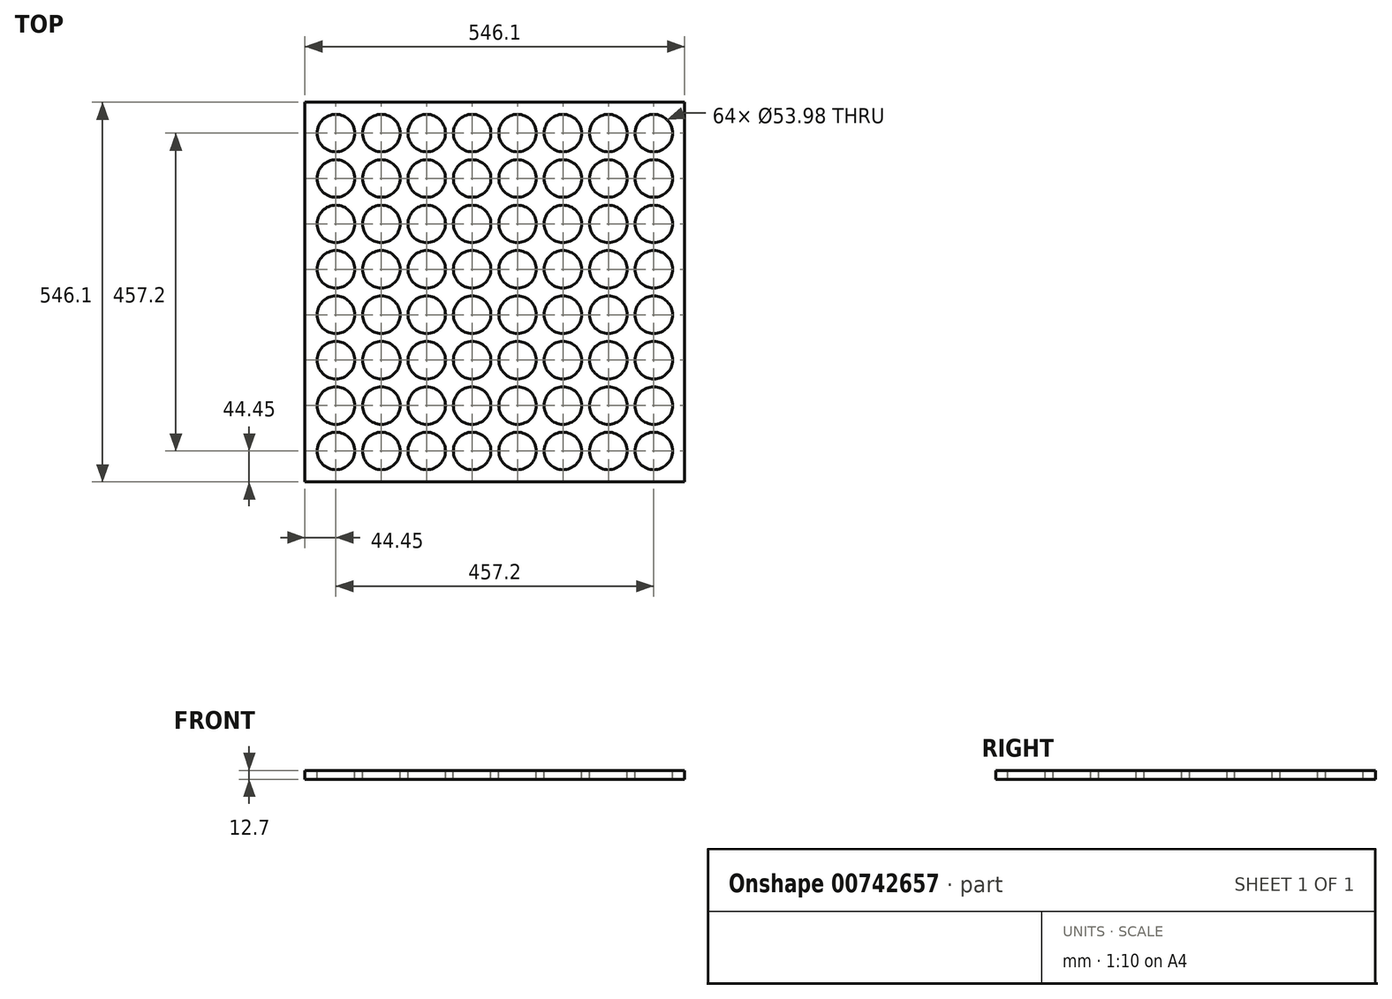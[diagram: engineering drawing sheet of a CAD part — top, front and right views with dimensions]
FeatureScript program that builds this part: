
annotation { "Feature Type Name" : "Feature", "Feature Type Description" : "" }
export const myFeature = defineFeature(function(context is Context, id is Id, definition is map)
    precondition{}
    {
        {
            var Q0;
            Q0=qCreatedBy(makeId("Top.planeOp"),FACE);
            var sketch = newSketch(context, id + "F0", { "sketchPlane" : qUnion([Q0])});
            skLineSegment(sketch, "E0.bottom", {"start": v(-273.05, 273.05) * mm, "end": v(273.05, 273.05) * mm});
            skLineSegment(sketch, "E0.top", {"start": v(-273.05, -273.05) * mm, "end": v(273.05, -273.05) * mm});
            skLineSegment(sketch, "E0.left", {"start": v(-273.05, 273.05) * mm, "end": v(-273.05, -273.05) * mm});
            skLineSegment(sketch, "E0.right", {"start": v(273.05, 273.05) * mm, "end": v(273.05, -273.05) * mm});
            skPoint(sketch, "E0.middle", {"position": v(0, 0) * mm});
            skSolve(sketch);
        }
        {
            var Q0;
            Q0=makeQuery(id+"F0.imprint","IMPRINT",FACE,{"disambiguationData":[TD([[makeQuery(id+"F0.imprint","IMPRINT",EDGE,{"derivedFrom":sQuery(id+"F0.wireOp",EDGE,"E0.bottom")}),-1.0]])]});
            extrude(context, id + "F1", {"entities" : qUnion([Q0]), "depth" : 12.7 * mm, "offsetDistance" : 25.4 * mm});
        }
        {
            var Q0;
            Q0=makeQuery(id+"F1.opExtrude","CAP_FACE",FACE,{"disambiguationData":[OSD([sQuery(id+"F0.wireOp",EDGE,"E0.bottom"),sQuery(id+"F0.wireOp",EDGE,"E0.top"),sQuery(id+"F0.wireOp",EDGE,"E0.left"),sQuery(id+"F0.wireOp",EDGE,"E0.right")])],"isStart":false});
            var sketch = newSketch(context, id + "F2", { "sketchPlane" : qUnion([Q0])});
            skCircle(sketch, "E1", {"center": v(-228.6, 228.6) * mm, "radius": 26.99 * mm});
            skCircle(sketch, "E2.0.1.0", {"center": v(-228.6, 163.29) * mm, "radius": 26.99 * mm});
            skCircle(sketch, "E2.0.2.0", {"center": v(-228.6, 97.97) * mm, "radius": 26.99 * mm});
            skCircle(sketch, "E2.0.3.0", {"center": v(-228.6, 32.66) * mm, "radius": 26.99 * mm});
            skCircle(sketch, "E2.0.4.0", {"center": v(-228.6, -32.66) * mm, "radius": 26.99 * mm});
            skCircle(sketch, "E2.0.5.0", {"center": v(-228.6, -97.97) * mm, "radius": 26.99 * mm});
            skCircle(sketch, "E2.0.6.0", {"center": v(-228.6, -163.29) * mm, "radius": 26.99 * mm});
            skCircle(sketch, "E2.0.7.0", {"center": v(-228.6, -228.6) * mm, "radius": 26.99 * mm});
            skCircle(sketch, "E2.1.0.0", {"center": v(-163.29, 228.6) * mm, "radius": 26.99 * mm});
            skCircle(sketch, "E2.1.1.0", {"center": v(-163.29, 163.29) * mm, "radius": 26.99 * mm});
            skCircle(sketch, "E2.1.2.0", {"center": v(-163.29, 97.97) * mm, "radius": 26.99 * mm});
            skCircle(sketch, "E2.1.3.0", {"center": v(-163.29, 32.66) * mm, "radius": 26.99 * mm});
            skCircle(sketch, "E2.1.4.0", {"center": v(-163.29, -32.66) * mm, "radius": 26.99 * mm});
            skCircle(sketch, "E2.1.5.0", {"center": v(-163.29, -97.97) * mm, "radius": 26.99 * mm});
            skCircle(sketch, "E2.1.6.0", {"center": v(-163.29, -163.29) * mm, "radius": 26.99 * mm});
            skCircle(sketch, "E2.1.7.0", {"center": v(-163.29, -228.6) * mm, "radius": 26.99 * mm});
            skCircle(sketch, "E2.2.0.0", {"center": v(-97.97, 228.6) * mm, "radius": 26.99 * mm});
            skCircle(sketch, "E2.2.1.0", {"center": v(-97.97, 163.29) * mm, "radius": 26.99 * mm});
            skCircle(sketch, "E2.2.2.0", {"center": v(-97.97, 97.97) * mm, "radius": 26.99 * mm});
            skCircle(sketch, "E2.2.3.0", {"center": v(-97.97, 32.66) * mm, "radius": 26.99 * mm});
            skCircle(sketch, "E2.2.4.0", {"center": v(-97.97, -32.66) * mm, "radius": 26.99 * mm});
            skCircle(sketch, "E2.2.5.0", {"center": v(-97.97, -97.97) * mm, "radius": 26.99 * mm});
            skCircle(sketch, "E2.2.6.0", {"center": v(-97.97, -163.29) * mm, "radius": 26.99 * mm});
            skCircle(sketch, "E2.2.7.0", {"center": v(-97.97, -228.6) * mm, "radius": 26.99 * mm});
            skCircle(sketch, "E2.3.0.0", {"center": v(-32.66, 228.6) * mm, "radius": 26.99 * mm});
            skCircle(sketch, "E2.3.1.0", {"center": v(-32.66, 163.29) * mm, "radius": 26.99 * mm});
            skCircle(sketch, "E2.3.2.0", {"center": v(-32.66, 97.97) * mm, "radius": 26.99 * mm});
            skCircle(sketch, "E2.3.3.0", {"center": v(-32.66, 32.66) * mm, "radius": 26.99 * mm});
            skCircle(sketch, "E2.3.4.0", {"center": v(-32.66, -32.66) * mm, "radius": 26.99 * mm});
            skCircle(sketch, "E2.3.5.0", {"center": v(-32.66, -97.97) * mm, "radius": 26.99 * mm});
            skCircle(sketch, "E2.3.6.0", {"center": v(-32.66, -163.29) * mm, "radius": 26.99 * mm});
            skCircle(sketch, "E2.3.7.0", {"center": v(-32.66, -228.6) * mm, "radius": 26.99 * mm});
            skCircle(sketch, "E2.4.0.0", {"center": v(32.66, 228.6) * mm, "radius": 26.99 * mm});
            skCircle(sketch, "E2.4.1.0", {"center": v(32.66, 163.29) * mm, "radius": 26.99 * mm});
            skCircle(sketch, "E2.4.2.0", {"center": v(32.66, 97.97) * mm, "radius": 26.99 * mm});
            skCircle(sketch, "E2.4.3.0", {"center": v(32.66, 32.66) * mm, "radius": 26.99 * mm});
            skCircle(sketch, "E2.4.4.0", {"center": v(32.66, -32.66) * mm, "radius": 26.99 * mm});
            skCircle(sketch, "E2.4.5.0", {"center": v(32.66, -97.97) * mm, "radius": 26.99 * mm});
            skCircle(sketch, "E2.4.6.0", {"center": v(32.66, -163.29) * mm, "radius": 26.99 * mm});
            skCircle(sketch, "E2.4.7.0", {"center": v(32.66, -228.6) * mm, "radius": 26.99 * mm});
            skCircle(sketch, "E2.5.0.0", {"center": v(97.97, 228.6) * mm, "radius": 26.99 * mm});
            skCircle(sketch, "E2.5.1.0", {"center": v(97.97, 163.29) * mm, "radius": 26.99 * mm});
            skCircle(sketch, "E2.5.2.0", {"center": v(97.97, 97.97) * mm, "radius": 26.99 * mm});
            skCircle(sketch, "E2.5.3.0", {"center": v(97.97, 32.66) * mm, "radius": 26.99 * mm});
            skCircle(sketch, "E2.5.4.0", {"center": v(97.97, -32.66) * mm, "radius": 26.99 * mm});
            skCircle(sketch, "E2.5.5.0", {"center": v(97.97, -97.97) * mm, "radius": 26.99 * mm});
            skCircle(sketch, "E2.5.6.0", {"center": v(97.97, -163.29) * mm, "radius": 26.99 * mm});
            skCircle(sketch, "E2.5.7.0", {"center": v(97.97, -228.6) * mm, "radius": 26.99 * mm});
            skCircle(sketch, "E2.6.0.0", {"center": v(163.29, 228.6) * mm, "radius": 26.99 * mm});
            skCircle(sketch, "E2.6.1.0", {"center": v(163.29, 163.29) * mm, "radius": 26.99 * mm});
            skCircle(sketch, "E2.6.2.0", {"center": v(163.29, 97.97) * mm, "radius": 26.99 * mm});
            skCircle(sketch, "E2.6.3.0", {"center": v(163.29, 32.66) * mm, "radius": 26.99 * mm});
            skCircle(sketch, "E2.6.4.0", {"center": v(163.29, -32.66) * mm, "radius": 26.99 * mm});
            skCircle(sketch, "E2.6.5.0", {"center": v(163.29, -97.97) * mm, "radius": 26.99 * mm});
            skCircle(sketch, "E2.6.6.0", {"center": v(163.29, -163.29) * mm, "radius": 26.99 * mm});
            skCircle(sketch, "E2.6.7.0", {"center": v(163.29, -228.6) * mm, "radius": 26.99 * mm});
            skCircle(sketch, "E2.7.0.0", {"center": v(228.6, 228.6) * mm, "radius": 26.99 * mm});
            skCircle(sketch, "E2.7.1.0", {"center": v(228.6, 163.29) * mm, "radius": 26.99 * mm});
            skCircle(sketch, "E2.7.2.0", {"center": v(228.6, 97.97) * mm, "radius": 26.99 * mm});
            skCircle(sketch, "E2.7.3.0", {"center": v(228.6, 32.66) * mm, "radius": 26.99 * mm});
            skCircle(sketch, "E2.7.4.0", {"center": v(228.6, -32.66) * mm, "radius": 26.99 * mm});
            skCircle(sketch, "E2.7.5.0", {"center": v(228.6, -97.97) * mm, "radius": 26.99 * mm});
            skCircle(sketch, "E2.7.6.0", {"center": v(228.6, -163.29) * mm, "radius": 26.99 * mm});
            skCircle(sketch, "E2.7.7.0", {"center": v(228.6, -228.6) * mm, "radius": 26.99 * mm});
            skLineSegment(sketch, "E2.direction1", {"start": v(-228.6, 228.6) * mm, "end": v(-162.56, 228.6) * mm, "construction": true});
            skLineSegment(sketch, "E2.direction2", {"start": v(-228.6, 228.6) * mm, "end": v(-228.6, 162.56) * mm, "construction": true});
            skSolve(sketch);
        }
        {
            var Q0;
            Q0 = qSketchRegion(id + "F2", true);
            extrude(context, id + "F3", {"entities" : qUnion([Q0]), "operationType" : NewBodyOperationType.REMOVE, "endBound" : BoundingType.SYMMETRIC, "oppositeDirection" : true, "depth" : 25.4 * mm, "offsetDistance" : 25.4 * mm});
        }
    });
